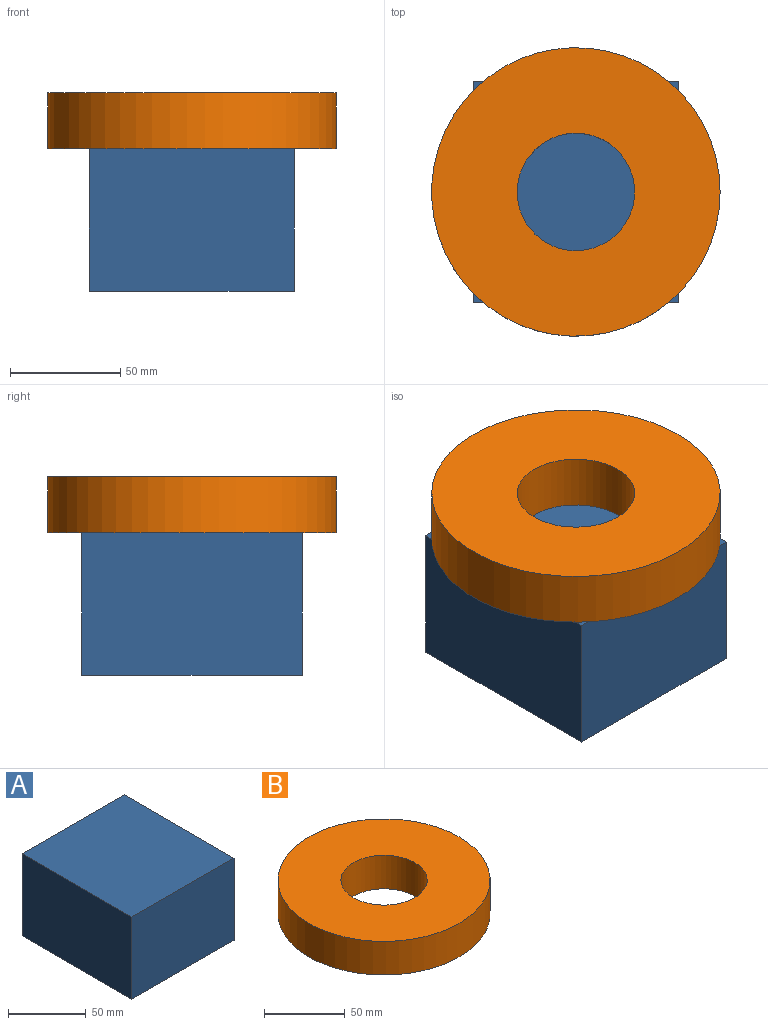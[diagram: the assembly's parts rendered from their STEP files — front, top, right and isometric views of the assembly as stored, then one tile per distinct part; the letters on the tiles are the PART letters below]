
ASSEMBLY  parts=2 mates=1
PART A: 6 faces, bbox 93x100x64.7 mm
  f0: plane 100x92.98mm, normal (0,0,1), area 9298.1mm2, adj f1,f3,f4,f5
  f1: plane 100x64.73mm, normal (-1,0,0), area 6472.7mm2, adj f0,f2,f4,f5
  f2: plane 100x92.98mm, normal (0,0,-1), area 9298.1mm2, adj f1,f3,f4,f5
  f3: plane 100x64.73mm, normal (1,0,0), area 6472.7mm2, adj f0,f2,f4,f5
  f4: plane 92.98x64.73mm, normal (0,-1,0), area 6018.4mm2, adj f0,f1,f2,f3
  f5: plane 92.98x64.73mm, normal (0,1,0), area 6018.4mm2, adj f0,f1,f2,f3
PART B: 4 faces, bbox 131x131x25.4 mm
  f0: cylinder r=26.67mm len=53.34mm, axis (0,0,-1), area 4256.3mm2, adj f2,f3
  f1: cylinder r=65.51mm len=131.01mm, axis (0,0,-1), area 10454.4mm2, adj f2,f3
  f2: plane 131.01x131.01mm, normal (0,0,1), area 11246.4mm2, adj f0,f1
  f3: plane 131.01x131.01mm, normal (0,0,-1), area 11246.4mm2, adj f0,f1
PLACE A t=(-61.42,23.67,-18.12)mm
PLACE B t=(-62.06,-26.33,46.61)mm
MATE fastened B.f1 <-> A.f0  axis (0,0,-1) through (-62.06,-26.33,46.61)mm
